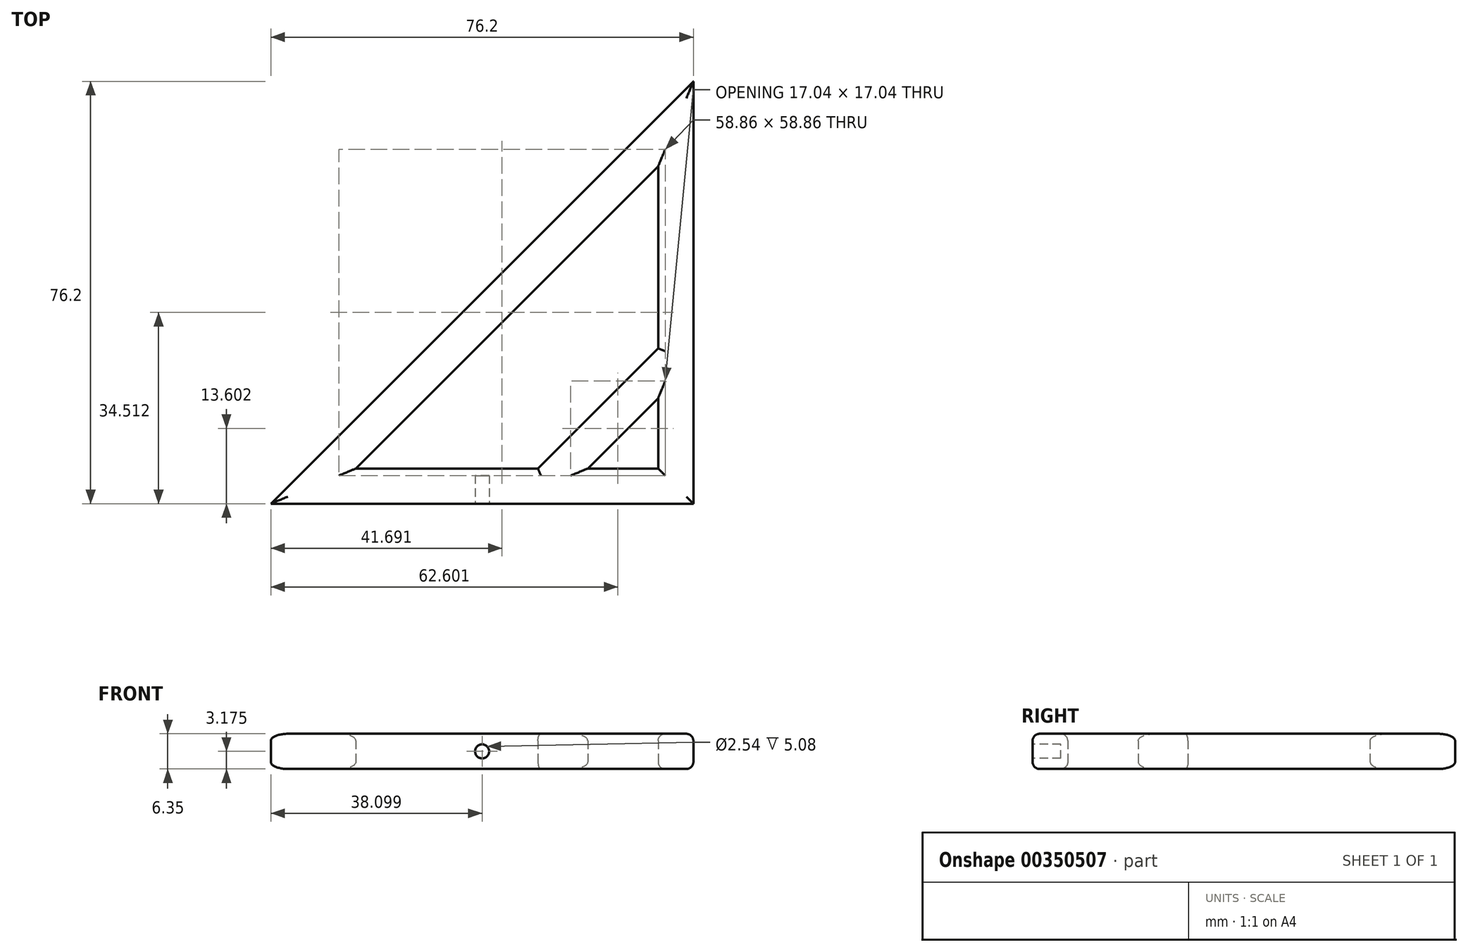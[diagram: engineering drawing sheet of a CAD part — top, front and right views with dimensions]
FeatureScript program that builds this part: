
annotation { "Feature Type Name" : "Feature", "Feature Type Description" : "" }
export const myFeature = defineFeature(function(context is Context, id is Id, definition is map)
    precondition{}
    {
        {
            var Q0;
            Q0=qCreatedBy(makeId("Top.planeOp"),FACE);
            var sketch = newSketch(context, id + "F0", { "sketchPlane" : qUnion([Q0])});
            skLineSegment(sketch, "E0", {"start": v(-52.02, -23.26) * mm, "end": v(24.18, -23.26) * mm});
            skLineSegment(sketch, "E1", {"start": v(24.18, -23.26) * mm, "end": v(24.18, 52.94) * mm});
            skLineSegment(sketch, "E2", {"start": v(24.18, 52.94) * mm, "end": v(-52.02, -23.26) * mm});
            skLineSegment(sketch, "E3", {"start": v(-36.7, -16.9) * mm, "end": v(17.83, 37.61) * mm});
            skLineSegment(sketch, "E4", {"start": v(5.13, -16.9) * mm, "end": v(17.83, -4.2) * mm});
            skLineSegment(sketch, "E5", {"start": v(-3.85, -16.9) * mm, "end": v(17.83, 4.77) * mm});
            skLineSegment(sketch, "E6", {"start": v(-3.85, -16.9) * mm, "end": v(-36.7, -16.9) * mm});
            skLineSegment(sketch, "E7", {"start": v(5.13, -16.9) * mm, "end": v(17.83, -16.9) * mm});
            skLineSegment(sketch, "E8", {"start": v(17.83, -16.9) * mm, "end": v(17.83, -4.2) * mm});
            skLineSegment(sketch, "E9", {"start": v(17.83, 4.77) * mm, "end": v(17.83, 37.61) * mm});
            skSolve(sketch);
        }
        {
            var Q0;
            Q0=makeQuery(id+"F0.imprint","IMPRINT",FACE,{"disambiguationData":[TD([[makeQuery(id+"F0.imprint","IMPRINT",EDGE,{"derivedFrom":sQuery(id+"F0.wireOp",EDGE,"E0")}),1.0]])]});
            extrude(context, id + "F1", {"entities" : qUnion([Q0]), "depth" : 6.35 * mm});
        }
        {
            var Q0;
            Q0=makeQuery(id+"F1.opExtrude","SWEPT_FACE",FACE,{"disambiguationData":[OSD([sQuery(id+"F0.wireOp",EDGE,"E0")])]});
            var sketch = newSketch(context, id + "F2", { "sketchPlane" : qUnion([Q0])});
            skCircle(sketch, "E10", {"center": v(-13.92, 3.18) * mm, "radius": 1.27 * mm});
            skSolve(sketch);
        }
        {
            var Q0;
            Q0=makeQuery(id+"F1.opExtrude","CAP_FACE",FACE,{"disambiguationData":[OSD([sQuery(id+"F0.wireOp",EDGE,"E0"),sQuery(id+"F0.wireOp",EDGE,"E1"),sQuery(id+"F0.wireOp",EDGE,"E2"),sQuery(id+"F0.wireOp",EDGE,"E3"),sQuery(id+"F0.wireOp",EDGE,"E4"),sQuery(id+"F0.wireOp",EDGE,"E5"),sQuery(id+"F0.wireOp",EDGE,"E6"),sQuery(id+"F0.wireOp",EDGE,"E7"),sQuery(id+"F0.wireOp",EDGE,"E8"),sQuery(id+"F0.wireOp",EDGE,"E9")])],"isStart":false});
            var Q1;
            Q1=makeQuery(id+"F1.opExtrude","CAP_EDGE",EDGE,{"disambiguationData":[OSD([sQuery(id+"F0.wireOp",EDGE,"E0")])],"isStart":true});
            var Q2;
            Q2=makeQuery(id+"F1.opExtrude","CAP_FACE",FACE,{"disambiguationData":[OSD([sQuery(id+"F0.wireOp",EDGE,"E0"),sQuery(id+"F0.wireOp",EDGE,"E1"),sQuery(id+"F0.wireOp",EDGE,"E2"),sQuery(id+"F0.wireOp",EDGE,"E3"),sQuery(id+"F0.wireOp",EDGE,"E4"),sQuery(id+"F0.wireOp",EDGE,"E5"),sQuery(id+"F0.wireOp",EDGE,"E6"),sQuery(id+"F0.wireOp",EDGE,"E7"),sQuery(id+"F0.wireOp",EDGE,"E8"),sQuery(id+"F0.wireOp",EDGE,"E9")])],"isStart":true});
            fillet(context, id + "F3", {"entities" : qUnion([Q0, Q1, Q2]), "radius" : 1.27 * mm, "tangentPropagation" : true, "allowEdgeOverflow" : false});
        }
        {
            var Q0;
            Q0=makeQuery(id+"F2.imprint","IMPRINT",FACE,{"disambiguationData":[TD([[makeQuery(id+"F2.imprint","IMPRINT",EDGE,{"derivedFrom":sQuery(id+"F2.wireOp",EDGE,"E10")}),1.0]])]});
            extrude(context, id + "F4", {"entities" : qUnion([Q0]), "operationType" : NewBodyOperationType.REMOVE, "oppositeDirection" : true, "depth" : 5.08 * mm});
        }
    });
